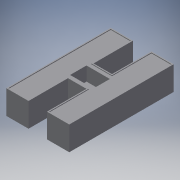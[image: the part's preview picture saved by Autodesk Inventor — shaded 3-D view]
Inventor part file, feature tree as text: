
AUTODESK INVENTOR PART (.ipt)
format: ipt  version: 2018.3 (Build 223284000, 284)  size: 208,384 bytes
history: native  units: mm
features: extrude x8, sketch x8
ambient origin geometry x8: Origin, YZ Plane, XZ Plane, XY Plane, X Axis, Y Axis, Z Axis, Center Point
bodies: Solid1 (feature_tree)
feature tree (16):
  extrude  "Extrusion1"  Depth=19.2mm
  extrude  "Extrusion2"  Depth=15.87mm
  extrude  "Extrusion3"  Depth=34.0mm
  extrude  "Extrusion4"  Depth=6.9mm
  extrude  "Extrusion5"  Depth=27.15mm TaperAngle=0.0deg
  extrude  "Extrusion6"  Depth=14.549065mm
  extrude  "Extrusion7"  Depth=4.29mm TaperAngle=0.0deg
  extrude  "Extrusion8"  Depth=4.29mm
  sketch  "Sketch1"  dims[d0=90.0mm d1=19.2mm]
  sketch  "Sketch2"  dims[d2=34.0mm d3=15.87mm]
  sketch  "Sketch3"  dims[d4=19.2mm d5=34.0mm]
  sketch  "Sketch4"  dims[d6=20.67mm d7=0.0mm d8=6.9mm]
  sketch  "Sketch5"  dims[d9=4.29mm d10=27.15mm d11=0.0mm]
  sketch  "Sketch6"  dims[d12=24.88mm d13=14.549065mm]
  sketch  "Sketch7"  dims[d14=2.877mm d15=4.29mm d16=0.0mm]
  sketch  "Sketch8"  dims[d17=6.9mm d18=4.29mm d19=4.48mm d20=18.76mm d21=0.0mm d22=16.68mm d23=1.61mm d24=2.877mm d25=4.29mm d26=0.0mm d27=88.14mm d28=17.34mm d29=34.0mm d30=17.73mm d31=34.0mm d32=17.34mm d33=88.14mm d34=34.0mm d35=0.62mm d36=0.0mm d37=22.0mm d38=0.93mm d39=0.93mm d40=14.1mm d41=20.1mm d42=3.02mm d43=3.02mm d44=16.15mm d45=16.16mm d46=12.0mm d47=0.0mm d48=11.0mm d49=2.6mm d50=5.7mm d51=4.5mm d52=12.0mm d53=0.0mm]
